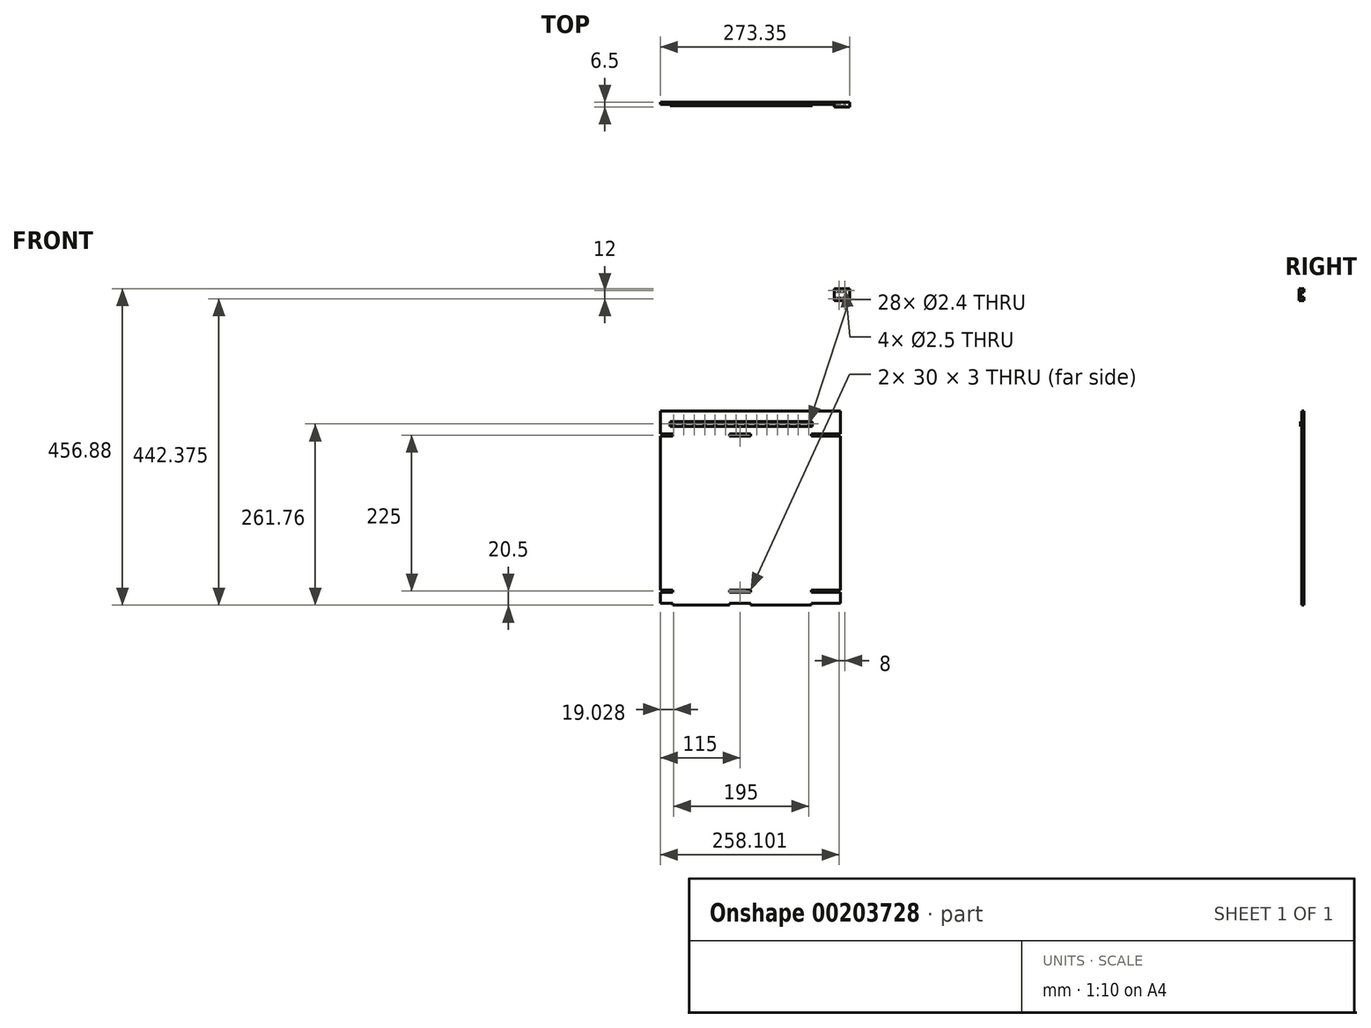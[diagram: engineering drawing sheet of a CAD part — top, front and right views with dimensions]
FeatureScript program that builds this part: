
annotation { "Feature Type Name" : "Feature", "Feature Type Description" : "" }
export const myFeature = defineFeature(function(context is Context, id is Id, definition is map)
    precondition{}
    {
        {
            var Q0;
            Q0=qCreatedBy(makeId("Front.planeOp"),FACE);
            var sketch = newSketch(context, id + "F0", { "sketchPlane" : qUnion([Q0])});
            skLineSegment(sketch, "E0.bottom", {"start": v(-130, 140) * mm, "end": v(130, 140) * mm});
            skLineSegment(sketch, "E0.top", {"start": v(-130, -140) * mm, "end": v(130, -140) * mm});
            skLineSegment(sketch, "E0.left", {"start": v(-130, 140) * mm, "end": v(-130, -140) * mm});
            skLineSegment(sketch, "E0.right", {"start": v(130, 140) * mm, "end": v(130, -140) * mm});
            skPoint(sketch, "E0.middle", {"position": v(0, 0) * mm});
            skPoint(sketch, "E1", {"position": v(-112, 140) * mm});
            skPoint(sketch, "E2", {"position": v(88, 140) * mm});
            skPoint(sketch, "E3", {"position": v(-130, 107) * mm});
            skPoint(sketch, "E4", {"position": v(-130, 134.5) * mm});
            skLineSegment(sketch, "E5", {"start": v(-130, 104) * mm, "end": v(-112, 104) * mm});
            skLineSegment(sketch, "E6", {"start": v(88, 104) * mm, "end": v(88, 55.2) * mm, "construction": true});
            skLineSegment(sketch, "E7", {"start": v(88, 55.2) * mm, "end": v(130, 55.2) * mm, "construction": true});
            skLineSegment(sketch, "E8", {"start": v(85, 104) * mm, "end": v(85, -140) * mm});
            skLineSegment(sketch, "E9", {"start": v(88, 104) * mm, "end": v(88, -140) * mm});
            skLineSegment(sketch, "E10.bottom", {"start": v(-112, 104) * mm, "end": v(-112, 104) * mm});
            skLineSegment(sketch, "E10.left", {"start": v(-112, 104) * mm, "end": v(-112, 107) * mm});
            skLineSegment(sketch, "E10.right", {"start": v(-112, 104) * mm, "end": v(-112, 107) * mm});
            skPoint(sketch, "E10.middle", {"position": v(-112, 107) * mm});
            skLineSegment(sketch, "E11", {"start": v(88, 104) * mm, "end": v(88, 107) * mm});
            skLineSegment(sketch, "E12", {"start": v(0, 107) * mm, "end": v(-30, 107) * mm});
            skLineSegment(sketch, "E13", {"start": v(-30, 107) * mm, "end": v(-30, 104) * mm});
            skLineSegment(sketch, "E14", {"start": v(0, 107) * mm, "end": v(0, 104) * mm});
            skLineSegment(sketch, "E15", {"start": v(88, 107) * mm, "end": v(130, 107) * mm});
            skLineSegment(sketch, "E16", {"start": v(-112, 107) * mm, "end": v(-130, 107) * mm});
            skLineSegment(sketch, "E17.trimOffspring", {"start": v(-30, 104) * mm, "end": v(0, 104) * mm});
            skLineSegment(sketch, "E18.trimOffspring", {"start": v(85, 104) * mm, "end": v(130, 104) * mm});
            skCircle(sketch, "E19", {"center": v(-110.97, 121.76) * mm, "radius": 1.2 * mm});
            skCircle(sketch, "E20.1.0.0", {"center": v(-95.97, 121.76) * mm, "radius": 1.2 * mm});
            skCircle(sketch, "E20.2.0.0", {"center": v(-80.97, 121.76) * mm, "radius": 1.2 * mm});
            skCircle(sketch, "E20.3.0.0", {"center": v(-65.97, 121.76) * mm, "radius": 1.2 * mm});
            skCircle(sketch, "E20.4.0.0", {"center": v(-50.97, 121.76) * mm, "radius": 1.2 * mm});
            skCircle(sketch, "E20.5.0.0", {"center": v(-35.97, 121.76) * mm, "radius": 1.2 * mm});
            skCircle(sketch, "E20.6.0.0", {"center": v(-20.97, 121.76) * mm, "radius": 1.2 * mm});
            skCircle(sketch, "E20.7.0.0", {"center": v(-5.97, 121.76) * mm, "radius": 1.2 * mm});
            skCircle(sketch, "E20.8.0.0", {"center": v(9.03, 121.76) * mm, "radius": 1.2 * mm});
            skCircle(sketch, "E20.9.0.0", {"center": v(24.03, 121.76) * mm, "radius": 1.2 * mm});
            skCircle(sketch, "E20.10.0.0", {"center": v(39.03, 121.76) * mm, "radius": 1.2 * mm});
            skCircle(sketch, "E20.11.0.0", {"center": v(54.03, 121.76) * mm, "radius": 1.2 * mm});
            skLineSegment(sketch, "E20.direction1", {"start": v(-110.97, 121.76) * mm, "end": v(-95.97, 121.76) * mm, "construction": true});
            skPoint(sketch, "E21", {"position": v(130, -137) * mm});
            skPoint(sketch, "E22", {"position": v(130, -121) * mm});
            skLineSegment(sketch, "E23", {"start": v(130, -121) * mm, "end": v(-130, -121) * mm});
            skLineSegment(sketch, "E24", {"start": v(130, -118) * mm, "end": v(-130, -118) * mm});
            skLineSegment(sketch, "E25", {"start": v(130, -137) * mm, "end": v(-130, -137) * mm});
            skPoint(sketch, "E26.endSnap0", {"position": v(0, -140) * mm});
            skLineSegment(sketch, "E27", {"start": v(-30, -118) * mm, "end": v(-30, -121) * mm});
            skLineSegment(sketch, "E28.trimOffspring", {"start": v(0, -118) * mm, "end": v(0, -121) * mm});
            skLineSegment(sketch, "E29.trimOffspring", {"start": v(-30, -137) * mm, "end": v(-30, -140) * mm});
            skLineSegment(sketch, "E30.trimOffspring", {"start": v(0, -137) * mm, "end": v(0, -140) * mm});
            skPoint(sketch, "E31.orphan", {"position": v(0, -130.47) * mm});
            skPoint(sketch, "E32", {"position": v(-115.97, 137.77) * mm});
            skPoint(sketch, "E33", {"position": v(89.03, 105.75) * mm});
            skLineSegment(sketch, "E34.top", {"start": v(-115.97, 125.26) * mm, "end": v(89.03, 125.26) * mm});
            skLineSegment(sketch, "E35.MirrorCS", {"start": v(-115.97, 118.26) * mm, "end": v(89.03, 118.26) * mm});
            skLineSegment(sketch, "E36.MirrorCS", {"start": v(-115.97, 125.26) * mm, "end": v(-115.97, 118.26) * mm});
            skLineSegment(sketch, "E37.MirrorCS", {"start": v(89.03, 125.26) * mm, "end": v(89.03, 118.26) * mm});
            skLineSegment(sketch, "E38.bottom", {"start": v(120.85, 316.88) * mm, "end": v(143.35, 316.88) * mm});
            skLineSegment(sketch, "E38.top", {"start": v(120.85, 299.88) * mm, "end": v(143.35, 299.88) * mm});
            skLineSegment(sketch, "E38.left", {"start": v(120.85, 316.88) * mm, "end": v(120.85, 299.88) * mm});
            skLineSegment(sketch, "E38.right", {"start": v(143.35, 316.88) * mm, "end": v(143.35, 299.88) * mm});
            skLineSegment(sketch, "E39.bottom", {"start": v(120.85, 311.88) * mm, "end": v(143.35, 311.88) * mm});
            skLineSegment(sketch, "E39.top", {"start": v(120.85, 304.88) * mm, "end": v(143.35, 304.88) * mm});
            skLineSegment(sketch, "E39.left", {"start": v(120.85, 311.88) * mm, "end": v(120.85, 304.88) * mm});
            skLineSegment(sketch, "E39.right", {"start": v(143.35, 311.88) * mm, "end": v(143.35, 304.88) * mm});
            skPoint(sketch, "E39.middle", {"position": v(132.1, 308.38) * mm});
            skPoint(sketch, "E39.middle.positionSnap0", {"position": v(120.85, 308.38) * mm});
            skPoint(sketch, "E39.middle.positionSnap1", {"position": v(132.1, 299.88) * mm});
            skPoint(sketch, "E39.centerSnap0", {"position": v(120.85, 308.38) * mm});
            skPoint(sketch, "E39.centerSnap1", {"position": v(132.1, 299.88) * mm});
            skCircle(sketch, "E40.0.12.0", {"center": v(69.03, 121.76) * mm, "radius": 1.2 * mm});
            skCircle(sketch, "E40.0.13.0", {"center": v(84.03, 121.76) * mm, "radius": 1.2 * mm});
            skLineSegment(sketch, "E41", {"start": v(-112, -118) * mm, "end": v(-112, -121) * mm});
            skLineSegment(sketch, "E42", {"start": v(-112, -137) * mm, "end": v(-112, -140) * mm});
            skPoint(sketch, "E43", {"position": v(136.1, 314.38) * mm});
            skPoint(sketch, "E44", {"position": v(128.1, 314.38) * mm});
            skPoint(sketch, "E45", {"position": v(128.1, 302.38) * mm});
            skPoint(sketch, "E46", {"position": v(136.1, 302.38) * mm});
            skPoint(sketch, "E47.orphan", {"position": v(-115.97, 105.75) * mm});
            skSolve(sketch);
        }
        {
            var Q0;
            {var subQ0=sQuery(id+"F0.wireOp",EDGE,"E18.trimOffspring");var subQ1=sQuery(id+"F0.wireOp",EDGE,"E0.right");var subQ2=makeQuery(id+"F0.imprint","INTERSECT",VERTEX,{"derivedFrom":[subQ1,subQ0]});Q0=makeQuery(id+"F0.imprint","IMPRINT",FACE,{"disambiguationData":[TD([[makeQuery(id+"F0.imprint","IMPRINT",EDGE,{"disambiguationData":[TD([[subQ2,-1.0]])],"derivedFrom":subQ1}),-1.0]])]});}
            var Q1;
            {var subQ0=sQuery(id+"F0.wireOp",EDGE,"E23");var subQ1=sQuery(id+"F0.wireOp",EDGE,"E0.right");var subQ2=makeQuery(id+"F0.imprint","INTERSECT",VERTEX,{"derivedFrom":[subQ1,subQ0]});Q1=makeQuery(id+"F0.imprint","IMPRINT",FACE,{"disambiguationData":[TD([[makeQuery(id+"F0.imprint","IMPRINT",EDGE,{"disambiguationData":[TD([[subQ2,-1.0]])],"derivedFrom":subQ1}),-1.0]])]});}
            var Q2;
            {var subQ13=sQuery(id+"F0.wireOp",EDGE,"E0.bottom");Q2=makeQuery(id+"F0.imprint","IMPRINT",FACE,{"disambiguationData":[TD([[makeQuery(id+"F0.imprint","IMPRINT",EDGE,{"derivedFrom":subQ13}),-1.0]])]});}
            var Q3;
            {var subQ0=sQuery(id+"F0.wireOp",EDGE,"E8");var subQ1=sQuery(id+"F0.wireOp",EDGE,"E0.top");var subQ2=makeQuery(id+"F0.imprint","INTERSECT",VERTEX,{"derivedFrom":[subQ1,subQ0]});Q3=makeQuery(id+"F0.imprint","IMPRINT",FACE,{"disambiguationData":[TD([[makeQuery(id+"F0.imprint","IMPRINT",EDGE,{"disambiguationData":[TD([[subQ2,-1.0]])],"derivedFrom":subQ1}),1.0]])]});}
            var Q4;
            {var subQ0=sQuery(id+"F0.wireOp",EDGE,"E18.trimOffspring");var subQ1=sQuery(id+"F0.wireOp",EDGE,"E8");var subQ2=makeQuery(id+"F0.imprint","INTERSECT",VERTEX,{"derivedFrom":[subQ1,subQ0]});Q4=makeQuery(id+"F0.imprint","IMPRINT",FACE,{"disambiguationData":[TD([[makeQuery(id+"F0.imprint","IMPRINT",EDGE,{"disambiguationData":[TD([[subQ2,-1.0]])],"derivedFrom":subQ1}),1.0]])]});}
            var Q5;
            {var subQ0=sQuery(id+"F0.wireOp",EDGE,"E24");var subQ1=sQuery(id+"F0.wireOp",EDGE,"E8");var subQ2=makeQuery(id+"F0.imprint","INTERSECT",VERTEX,{"derivedFrom":[subQ1,subQ0]});Q5=makeQuery(id+"F0.imprint","IMPRINT",FACE,{"disambiguationData":[TD([[makeQuery(id+"F0.imprint","IMPRINT",EDGE,{"disambiguationData":[TD([[subQ2,-1.0]])],"derivedFrom":subQ1}),1.0]])]});}
            var Q6;
            {var subQ0=sQuery(id+"F0.wireOp",EDGE,"E23");var subQ1=sQuery(id+"F0.wireOp",EDGE,"E8");var subQ2=makeQuery(id+"F0.imprint","INTERSECT",VERTEX,{"derivedFrom":[subQ1,subQ0]});Q6=makeQuery(id+"F0.imprint","IMPRINT",FACE,{"disambiguationData":[TD([[makeQuery(id+"F0.imprint","IMPRINT",EDGE,{"disambiguationData":[TD([[subQ2,-1.0]])],"derivedFrom":subQ1}),1.0]])]});}
            var Q7;
            {var subQ0=sQuery(id+"F0.wireOp",EDGE,"E23");var subQ7=sQuery(id+"F0.wireOp",EDGE,"E0.left");var subQ8=makeQuery(id+"F0.imprint","INTERSECT",VERTEX,{"derivedFrom":[subQ7,subQ0]});Q7=makeQuery(id+"F0.imprint","IMPRINT",FACE,{"disambiguationData":[TD([[makeQuery(id+"F0.imprint","IMPRINT",EDGE,{"disambiguationData":[TD([[subQ8,-1.0]])],"derivedFrom":subQ7}),1.0]])]});}
            var Q8;
            {var subQ3=sQuery(id+"F0.wireOp",EDGE,"E29.trimOffspring");Q8=makeQuery(id+"F0.imprint","IMPRINT",FACE,{"disambiguationData":[TD([[makeQuery(id+"F0.imprint","IMPRINT",EDGE,{"derivedFrom":subQ3}),-1.0]])]});}
            var Q9;
            {var subQ3=sQuery(id+"F0.wireOp",EDGE,"E30.trimOffspring");Q9=makeQuery(id+"F0.imprint","IMPRINT",FACE,{"disambiguationData":[TD([[makeQuery(id+"F0.imprint","IMPRINT",EDGE,{"derivedFrom":subQ3}),1.0]])]});}
            var Q10;
            {var subQ5=sQuery(id+"F0.wireOp",EDGE,"E28.trimOffspring");Q10=makeQuery(id+"F0.imprint","IMPRINT",FACE,{"disambiguationData":[TD([[makeQuery(id+"F0.imprint","IMPRINT",EDGE,{"derivedFrom":subQ5}),1.0]])]});}
            var Q11;
            {var subQ5=sQuery(id+"F0.wireOp",EDGE,"E27");Q11=makeQuery(id+"F0.imprint","IMPRINT",FACE,{"disambiguationData":[TD([[makeQuery(id+"F0.imprint","IMPRINT",EDGE,{"derivedFrom":subQ5}),-1.0]])]});}
            var Q12;
            Q12=makeQuery(id+"F0.imprint","IMPRINT",FACE,{"disambiguationData":[TD([[makeQuery(id+"F0.imprint","IMPRINT",EDGE,{"derivedFrom":sQuery(id+"F0.wireOp",EDGE,"E19")}),-1.0]])]});
            extrude(context, id + "F1", {"entities" : qUnion([Q0, Q1, Q2, Q3, Q4, Q5, Q6, Q7, Q8, Q9, Q10, Q11, Q12]), "depth" : 3 * mm});
        }
        {
            var Q0;
            Q0=makeQuery(id+"F0.imprint","IMPRINT",FACE,{"disambiguationData":[TD([[makeQuery(id+"F0.imprint","IMPRINT",EDGE,{"derivedFrom":sQuery(id+"F0.wireOp",EDGE,"E19")}),-1.0]])]});
            extrude(context, id + "F2", {"entities" : qUnion([Q0]), "depth" : 4.8 * mm});
        }
        {
            var Q0;
            {var subQ0=sQuery(id+"F0.wireOp",EDGE,"E38.top");Q0=makeQuery(id+"F0.imprint","IMPRINT",FACE,{"disambiguationData":[TD([[makeQuery(id+"F0.imprint","IMPRINT",EDGE,{"derivedFrom":subQ0}),1.0]])]});}
            var Q1;
            Q1=makeQuery(id+"F0.imprint","IMPRINT",FACE,{"disambiguationData":[TD([[makeQuery(id+"F0.imprint","IMPRINT",EDGE,{"derivedFrom":sQuery(id+"F0.wireOp",EDGE,"E39.bottom")}),-1.0]])]});
            var Q2;
            {var subQ0=sQuery(id+"F0.wireOp",EDGE,"E38.bottom");Q2=makeQuery(id+"F0.imprint","IMPRINT",FACE,{"disambiguationData":[TD([[makeQuery(id+"F0.imprint","IMPRINT",EDGE,{"derivedFrom":subQ0}),-1.0]])]});}
            extrude(context, id + "F3", {"entities" : qUnion([Q0, Q1, Q2]), "depth" : 6.5 * mm});
        }
        {
            var Q0;
            Q0=makeQuery(id+"F0.imprint","IMPRINT",FACE,{"disambiguationData":[TD([[makeQuery(id+"F0.imprint","IMPRINT",EDGE,{"derivedFrom":sQuery(id+"F0.wireOp",EDGE,"E39.bottom")}),-1.0]])]});
            extrude(context, id + "F4", {"entities" : qUnion([Q0]), "operationType" : NewBodyOperationType.REMOVE, "depth" : 4 * mm});
        }
        {
            var Q0;
            Q0=sQuery(id+"F0.wireOp",VERTEX,"E43");
            var Q1;
            Q1=sQuery(id+"F0.wireOp",VERTEX,"E44");
            var Q2;
            Q2=sQuery(id+"F0.wireOp",VERTEX,"E45");
            var Q3;
            Q3=sQuery(id+"F0.wireOp",VERTEX,"E46");
            var Q4;
            Q4=makeQuery(id+"F3.opExtrude","SWEPT_BODY",BODY,{"disambiguationData":[OSD([sQuery(id+"F0.wireOp",EDGE,"E38.bottom"),sQuery(id+"F0.wireOp",EDGE,"E38.top"),sQuery(id+"F0.wireOp",EDGE,"E38.left"),sQuery(id+"F0.wireOp",EDGE,"E38.right"),sQuery(id+"F0.wireOp",EDGE,"E39.left"),sQuery(id+"F0.wireOp",EDGE,"E39.right")])]});
            hole(context, id + "F5", {"style" : HoleStyle.SIMPLE, "endStyle" : HoleEndStyle.BLIND, "oppositeDirection" : true, "holeDiameter" : 2.5 * mm, "holeDepth" : 800 * mm, "tappedDepth" : 12 * mm, "tapClearance" : 3, "locations" : qUnion([Q0, Q1, Q2, Q3]), "scope" : qUnion([Q4])});
        }
    });
